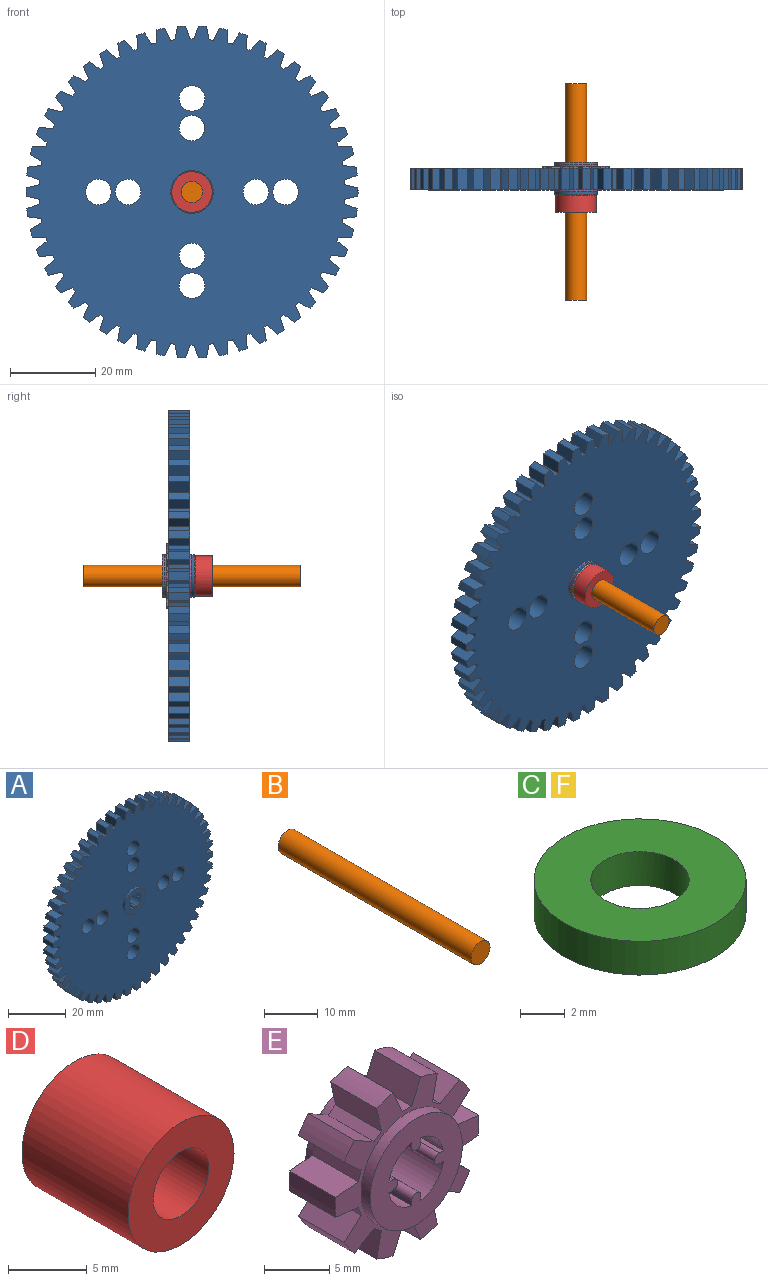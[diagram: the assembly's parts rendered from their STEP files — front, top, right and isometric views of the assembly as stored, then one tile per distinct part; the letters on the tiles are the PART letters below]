
ASSEMBLY  parts=6 mates=5
PART A: 230 faces, bbox 78x7x77.9 mm
  f0: plane 78x77.94mm, normal (0,1,0), area 4170.7mm2, adj f1,f3,f4,f5,f16,f26,f27,f28
  f1: cylinder r=3mm len=6mm, axis (0,1,0), area 94.2mm2, adj f0,f2
  f2: plane 78x77.94mm, normal (0,-1,0), area 4170.7mm2, adj f1,f3,f4,f5,f6,f26,f27,f28
  f3: cylinder r=3mm len=6mm, axis (0,1,0), area 94.2mm2, adj f0,f2
  f4: cylinder r=3mm len=6mm, axis (0,1,0), area 94.2mm2, adj f0,f2
  f5: cylinder r=3mm len=6mm, axis (0,1,0), area 94.2mm2, adj f0,f2
  f6: cylinder r=5mm len=10mm, axis (0,-1,0), area 31.4mm2, adj f2,f7
  f7: plane 10x10mm, normal (0,-1,0), area 53.8mm2, adj f6,f8,f9,f10,f11,f12,f13,f14
  f8: cylinder r=0.5mm len=7mm, axis (0,-1,0), area 11mm2, adj f7,f9,f14,f15
  f9: plane 7x0.46mm, normal (1,0,0), area 3.2mm2, adj f7,f8,f11,f15
  f10: cylinder r=3mm len=7mm, axis (0,1,0), area 26mm2, adj f7,f14,f15,f25
  f11: cylinder r=3mm len=7mm, axis (0,1,0), area 26mm2, adj f7,f9,f15,f17
  f12: cylinder r=3mm len=7mm, axis (0,1,0), area 26mm2, adj f7,f15,f19,f20
  f13: cylinder r=3mm len=7mm, axis (0,1,0), area 26mm2, adj f7,f15,f22,f23
  f14: plane 7x0.46mm, normal (-1,0,0), area 3.2mm2, adj f7,f8,f10,f15
  f15: plane 10x10mm, normal (0,1,0), area 53.8mm2, adj f8,f9,f10,f11,f12,f13,f14,f16
  f16: cylinder r=5mm len=10mm, axis (0,1,0), area 31.4mm2, adj f0,f15
  f17: plane 7x0.46mm, normal (0,0,1), area 3.2mm2, adj f7,f11,f15,f18
  f18: cylinder r=0.5mm len=7mm, axis (0,-1,0), area 11mm2, adj f7,f15,f17,f19
  f19: plane 7x0.46mm, normal (0,0,-1), area 3.2mm2, adj f7,f12,f15,f18
  f20: plane 7x0.46mm, normal (1,0,0), area 3.2mm2, adj f7,f12,f15,f21
  f21: cylinder r=0.5mm len=7mm, axis (0,-1,0), area 11mm2, adj f7,f15,f20,f22
  f22: plane 7x0.46mm, normal (-1,0,0), area 3.2mm2, adj f7,f13,f15,f21
  f23: plane 7x0.46mm, normal (0,0,-1), area 3.2mm2, adj f7,f13,f15,f24
  f24: cylinder r=0.5mm len=7mm, axis (0,-1,0), area 11mm2, adj f7,f15,f23,f25
  f25: plane 7x0.46mm, normal (0,0,1), area 3.2mm2, adj f7,f10,f15,f24
  f26: plane 5x0.99mm, normal (-0.13,0,0.99), area 5mm2, adj f0,f2,f27,f225
  f27: plane 5x3.1mm, normal (-0.98,0,0.19), area 15.8mm2, adj f0,f2,f26,f77
  f28: cylinder r=39mm len=5mm, axis (0,-1,0), area 9.5mm2, adj f0,f2,f78,f81
  f29: cylinder r=39mm len=5mm, axis (0,-1,0), area 9.5mm2, adj f0,f2,f80,f84
  f30: cylinder r=39mm len=5mm, axis (0,-1,0), area 9.5mm2, adj f0,f2,f86,f87
  f31: cylinder r=39mm len=5mm, axis (0,-1,0), area 9.5mm2, adj f0,f2,f89,f90
  f32: cylinder r=39mm len=5mm, axis (0,-1,0), area 9.5mm2, adj f0,f2,f92,f93
  f33: cylinder r=39mm len=5mm, axis (0,-1,0), area 9.5mm2, adj f0,f2,f95,f96
  f34: cylinder r=39mm len=5mm, axis (0,-1,0), area 9.5mm2, adj f0,f2,f98,f99
  f35: cylinder r=39mm len=5mm, axis (0,-1,0), area 9.5mm2, adj f0,f2,f101,f102
  f36: cylinder r=39mm len=5mm, axis (0,-1,0), area 9.5mm2, adj f0,f2,f104,f105
  f37: cylinder r=39mm len=5mm, axis (0,-1,0), area 9.5mm2, adj f0,f2,f107,f108
  f38: cylinder r=39mm len=5mm, axis (0,-1,0), area 9.5mm2, adj f0,f2,f110,f111
  f39: cylinder r=39mm len=5mm, axis (0,-1,0), area 9.5mm2, adj f0,f2,f113,f114
  f40: cylinder r=39mm len=5mm, axis (0,-1,0), area 9.5mm2, adj f0,f2,f116,f117
  f41: cylinder r=39mm len=5mm, axis (0,-1,0), area 9.5mm2, adj f0,f2,f119,f120
  f42: cylinder r=39mm len=5mm, axis (0,-1,0), area 9.5mm2, adj f0,f2,f122,f123
  f43: cylinder r=39mm len=5mm, axis (0,-1,0), area 9.5mm2, adj f0,f2,f125,f126
  f44: cylinder r=39mm len=5mm, axis (0,-1,0), area 9.5mm2, adj f0,f2,f128,f129
  f45: cylinder r=39mm len=5mm, axis (0,-1,0), area 9.5mm2, adj f0,f2,f131,f132
  f46: cylinder r=39mm len=5mm, axis (0,-1,0), area 9.5mm2, adj f0,f2,f134,f135
  f47: cylinder r=39mm len=5mm, axis (0,-1,0), area 9.5mm2, adj f0,f2,f137,f138
  f48: cylinder r=39mm len=5mm, axis (0,-1,0), area 9.5mm2, adj f0,f2,f140,f141
  f49: cylinder r=39mm len=5mm, axis (0,-1,0), area 9.5mm2, adj f0,f2,f143,f144
  f50: cylinder r=39mm len=5mm, axis (0,-1,0), area 9.5mm2, adj f0,f2,f146,f147
  f51: cylinder r=39mm len=5mm, axis (0,-1,0), area 9.5mm2, adj f0,f2,f149,f150
  f52: cylinder r=39mm len=5mm, axis (0,-1,0), area 9.5mm2, adj f0,f2,f152,f153
  f53: cylinder r=39mm len=5mm, axis (0,-1,0), area 9.5mm2, adj f0,f2,f155,f156
  f54: cylinder r=39mm len=5mm, axis (0,-1,0), area 9.5mm2, adj f0,f2,f158,f159
  f55: cylinder r=39mm len=5mm, axis (0,-1,0), area 9.5mm2, adj f0,f2,f161,f162
  f56: cylinder r=39mm len=5mm, axis (0,-1,0), area 9.5mm2, adj f0,f2,f164,f165
  f57: cylinder r=39mm len=5mm, axis (0,-1,0), area 9.5mm2, adj f0,f2,f167,f168
  f58: cylinder r=39mm len=5mm, axis (0,-1,0), area 9.5mm2, adj f0,f2,f170,f171
  f59: cylinder r=39mm len=5mm, axis (0,-1,0), area 9.5mm2, adj f0,f2,f173,f174
  f60: cylinder r=39mm len=5mm, axis (0,-1,0), area 9.5mm2, adj f0,f2,f176,f177
  f61: cylinder r=39mm len=5mm, axis (0,-1,0), area 9.5mm2, adj f0,f2,f179,f180
  f62: cylinder r=39mm len=5mm, axis (0,-1,0), area 9.5mm2, adj f0,f2,f182,f183
  f63: cylinder r=39mm len=5mm, axis (0,-1,0), area 9.5mm2, adj f0,f2,f185,f186
  f64: cylinder r=39mm len=5mm, axis (0,-1,0), area 9.5mm2, adj f0,f2,f188,f189
  f65: cylinder r=39mm len=5mm, axis (0,-1,0), area 9.5mm2, adj f0,f2,f191,f192
  f66: cylinder r=39mm len=5mm, axis (0,-1,0), area 9.5mm2, adj f0,f2,f194,f195
  f67: cylinder r=39mm len=5mm, axis (0,-1,0), area 9.5mm2, adj f0,f2,f197,f198
  f68: cylinder r=39mm len=5mm, axis (0,-1,0), area 9.5mm2, adj f0,f2,f200,f201
  f69: cylinder r=39mm len=5mm, axis (0,-1,0), area 9.5mm2, adj f0,f2,f203,f204
  f70: cylinder r=39mm len=5mm, axis (0,-1,0), area 9.5mm2, adj f0,f2,f206,f207
  f71: cylinder r=39mm len=5mm, axis (0,-1,0), area 9.5mm2, adj f0,f2,f209,f210
  f72: cylinder r=39mm len=5mm, axis (0,-1,0), area 9.5mm2, adj f0,f2,f212,f213
  f73: cylinder r=39mm len=5mm, axis (0,-1,0), area 9.5mm2, adj f0,f2,f215,f216
  f74: cylinder r=39mm len=5mm, axis (0,-1,0), area 9.5mm2, adj f0,f2,f218,f219
  f75: cylinder r=39mm len=5mm, axis (0,-1,0), area 9.5mm2, adj f0,f2,f221,f222
  f76: cylinder r=39mm len=5mm, axis (0,-1,0), area 9.5mm2, adj f0,f2,f224,f225
  f77: cylinder r=39mm len=5mm, axis (0,-1,0), area 9.5mm2, adj f0,f2,f27,f83
  f78: plane 5x3.1mm, normal (0.98,0,0.19), area 15.8mm2, adj f0,f2,f28,f79
  f79: plane 5x0.99mm, normal (0.13,0,0.99), area 5mm2, adj f0,f2,f78,f80
  f80: plane 5x2.85mm, normal (-0.9,0,0.43), area 15.8mm2, adj f0,f2,f29,f79
  f81: plane 5x3mm, normal (-0.95,0,0.32), area 15.8mm2, adj f0,f2,f28,f82
  f82: plane 5x1mm, normal (0,0,1), area 5mm2, adj f0,f2,f81,f83
  f83: plane 5x3mm, normal (0.95,0,0.32), area 15.8mm2, adj f0,f2,f77,f82
  f84: plane 5x3.15mm, normal (1,0,0.07), area 15.8mm2, adj f0,f2,f29,f85
  f85: plane 5x0.97mm, normal (0.25,0,0.97), area 5mm2, adj f0,f2,f84,f86
  f86: plane 5x2.66mm, normal (-0.84,0,0.54), area 15.8mm2, adj f0,f2,f30,f85
  f87: plane 5x3.16mm, normal (1,0,-0.06), area 15.8mm2, adj f0,f2,f30,f88
  f88: plane 5x0.93mm, normal (0.37,0,0.93), area 5mm2, adj f0,f2,f87,f89
  f89: plane 5x2.42mm, normal (-0.77,0,0.64), area 15.8mm2, adj f0,f2,f31,f88
  f90: plane 5x3.11mm, normal (0.98,0,-0.18), area 15.8mm2, adj f0,f2,f31,f91
  f91: plane 5x0.88mm, normal (0.48,0,0.88), area 5mm2, adj f0,f2,f90,f92
  f92: plane 5x2.32mm, normal (-0.68,0,0.73), area 15.8mm2, adj f0,f2,f32,f91
  f93: plane 5x3.02mm, normal (0.95,0,-0.3), area 15.8mm2, adj f0,f2,f32,f94
  f94: plane 5x0.81mm, normal (0.59,0,0.81), area 5mm2, adj f0,f2,f93,f95
  f95: plane 5x2.57mm, normal (-0.58,0,0.81), area 15.8mm2, adj f0,f2,f33,f94
  f96: plane 5x2.87mm, normal (0.91,0,-0.42), area 15.8mm2, adj f0,f2,f33,f97
  f97: plane 5x0.73mm, normal (0.68,0,0.73), area 5mm2, adj f0,f2,f96,f98
  f98: plane 5x2.78mm, normal (-0.48,0,0.88), area 15.8mm2, adj f0,f2,f34,f97
  f99: plane 5x2.68mm, normal (0.85,0,-0.53), area 15.8mm2, adj f0,f2,f34,f100
  f100: plane 5x0.77mm, normal (0.77,0,0.64), area 5mm2, adj f0,f2,f99,f101
  f101: plane 5x2.95mm, normal (-0.36,0,0.93), area 15.8mm2, adj f0,f2,f35,f100
  f102: plane 5x2.45mm, normal (0.78,0,-0.63), area 15.8mm2, adj f0,f2,f35,f103
  f103: plane 5x0.84mm, normal (0.84,0,0.54), area 5mm2, adj f0,f2,f102,f104
  f104: plane 5x3.07mm, normal (-0.24,0,0.97), area 15.8mm2, adj f0,f2,f36,f103
  f105: plane 5x2.29mm, normal (0.69,0,-0.72), area 15.8mm2, adj f0,f2,f36,f106
  f106: plane 5x0.91mm, normal (0.9,0,0.43), area 5mm2, adj f0,f2,f105,f107
  f107: plane 5x3.14mm, normal (-0.12,0,0.99), area 15.8mm2, adj f0,f2,f37,f106
  f108: plane 5x2.54mm, normal (0.59,0,-0.8), area 15.8mm2, adj f0,f2,f37,f109
  f109: plane 5x0.95mm, normal (0.95,0,0.31), area 5mm2, adj f0,f2,f108,f110
  f110: plane 5x3.16mm, normal (0.01,0,1), area 15.8mm2, adj f0,f2,f38,f109
  f111: plane 5x2.76mm, normal (0.49,0,-0.87), area 15.8mm2, adj f0,f2,f38,f112
  f112: plane 5x0.98mm, normal (0.98,0,0.19), area 5mm2, adj f0,f2,f111,f113
  f113: plane 5x3.13mm, normal (0.13,0,0.99), area 15.8mm2, adj f0,f2,f39,f112
  f114: plane 5x2.93mm, normal (0.38,0,-0.93), area 15.8mm2, adj f0,f2,f39,f115
  f115: plane 5x1mm, normal (1,0,0.06), area 5mm2, adj f0,f2,f114,f116
  f116: plane 5x3.06mm, normal (0.26,0,0.97), area 15.8mm2, adj f0,f2,f40,f115
  f117: plane 5x3.06mm, normal (0.26,0,-0.97), area 15.8mm2, adj f0,f2,f40,f118
  f118: plane 5x1mm, normal (1,0,-0.06), area 5mm2, adj f0,f2,f117,f119
  f119: plane 5x2.93mm, normal (0.38,0,0.93), area 15.8mm2, adj f0,f2,f41,f118
  f120: plane 5x3.13mm, normal (0.13,0,-0.99), area 15.8mm2, adj f0,f2,f41,f121
  f121: plane 5x0.98mm, normal (0.98,0,-0.19), area 5mm2, adj f0,f2,f120,f122
  f122: plane 5x2.76mm, normal (0.49,0,0.87), area 15.8mm2, adj f0,f2,f42,f121
  f123: plane 5x3.16mm, normal (0.01,0,-1), area 15.8mm2, adj f0,f2,f42,f124
  f124: plane 5x0.95mm, normal (0.95,0,-0.31), area 5mm2, adj f0,f2,f123,f125
  f125: plane 5x2.54mm, normal (0.59,0,0.8), area 15.8mm2, adj f0,f2,f43,f124
  f126: plane 5x3.14mm, normal (-0.12,0,-0.99), area 15.8mm2, adj f0,f2,f43,f127
  f127: plane 5x0.91mm, normal (0.9,0,-0.43), area 5mm2, adj f0,f2,f126,f128
  f128: plane 5x2.29mm, normal (0.69,0,0.72), area 15.8mm2, adj f0,f2,f44,f127
  f129: plane 5x3.07mm, normal (-0.24,0,-0.97), area 15.8mm2, adj f0,f2,f44,f130
  f130: plane 5x0.84mm, normal (0.84,0,-0.54), area 5mm2, adj f0,f2,f129,f131
  f131: plane 5x2.45mm, normal (0.78,0,0.63), area 15.8mm2, adj f0,f2,f45,f130
  f132: plane 5x2.95mm, normal (-0.36,0,-0.93), area 15.8mm2, adj f0,f2,f45,f133
  f133: plane 5x0.77mm, normal (0.77,0,-0.64), area 5mm2, adj f0,f2,f132,f134
  f134: plane 5x2.68mm, normal (0.85,0,0.53), area 15.8mm2, adj f0,f2,f46,f133
  f135: plane 5x2.78mm, normal (-0.48,0,-0.88), area 15.8mm2, adj f0,f2,f46,f136
  f136: plane 5x0.73mm, normal (0.68,0,-0.73), area 5mm2, adj f0,f2,f135,f137
  f137: plane 5x2.87mm, normal (0.91,0,0.42), area 15.8mm2, adj f0,f2,f47,f136
  f138: plane 5x2.57mm, normal (-0.58,0,-0.81), area 15.8mm2, adj f0,f2,f47,f139
  f139: plane 5x0.81mm, normal (0.59,0,-0.81), area 5mm2, adj f0,f2,f138,f140
  f140: plane 5x3.02mm, normal (0.95,0,0.3), area 15.8mm2, adj f0,f2,f48,f139
  f141: plane 5x2.32mm, normal (-0.68,0,-0.73), area 15.8mm2, adj f0,f2,f48,f142
  f142: plane 5x0.88mm, normal (0.48,0,-0.88), area 5mm2, adj f0,f2,f141,f143
  f143: plane 5x3.11mm, normal (0.98,0,0.18), area 15.8mm2, adj f0,f2,f49,f142
  f144: plane 5x2.42mm, normal (-0.77,0,-0.64), area 15.8mm2, adj f0,f2,f49,f145
  f145: plane 5x0.93mm, normal (0.37,0,-0.93), area 5mm2, adj f0,f2,f144,f146
  f146: plane 5x3.16mm, normal (1,0,0.06), area 15.8mm2, adj f0,f2,f50,f145
  f147: plane 5x2.66mm, normal (-0.84,0,-0.54), area 15.8mm2, adj f0,f2,f50,f148
  f148: plane 5x0.97mm, normal (0.25,0,-0.97), area 5mm2, adj f0,f2,f147,f149
  f149: plane 5x3.15mm, normal (1,0,-0.07), area 15.8mm2, adj f0,f2,f51,f148
  f150: plane 5x2.85mm, normal (-0.9,0,-0.43), area 15.8mm2, adj f0,f2,f51,f151
  f151: plane 5x0.99mm, normal (0.13,0,-0.99), area 5mm2, adj f0,f2,f150,f152
  f152: plane 5x3.1mm, normal (0.98,0,-0.19), area 15.8mm2, adj f0,f2,f52,f151
  f153: plane 5x3mm, normal (-0.95,0,-0.32), area 15.8mm2, adj f0,f2,f52,f154
  f154: plane 5x1mm, normal (0,0,-1), area 5mm2, adj f0,f2,f153,f155
  f155: plane 5x3mm, normal (0.95,0,-0.32), area 15.8mm2, adj f0,f2,f53,f154
  f156: plane 5x3.1mm, normal (-0.98,0,-0.19), area 15.8mm2, adj f0,f2,f53,f157
  f157: plane 5x0.99mm, normal (-0.13,0,-0.99), area 5mm2, adj f0,f2,f156,f158
  f158: plane 5x2.85mm, normal (0.9,0,-0.43), area 15.8mm2, adj f0,f2,f54,f157
  f159: plane 5x3.15mm, normal (-1,0,-0.07), area 15.8mm2, adj f0,f2,f54,f160
  f160: plane 5x0.97mm, normal (-0.25,0,-0.97), area 5mm2, adj f0,f2,f159,f161
  f161: plane 5x2.66mm, normal (0.84,0,-0.54), area 15.8mm2, adj f0,f2,f55,f160
  f162: plane 5x3.16mm, normal (-1,0,0.06), area 15.8mm2, adj f0,f2,f55,f163
  f163: plane 5x0.93mm, normal (-0.37,0,-0.93), area 5mm2, adj f0,f2,f162,f164
  f164: plane 5x2.42mm, normal (0.77,0,-0.64), area 15.8mm2, adj f0,f2,f56,f163
  f165: plane 5x3.11mm, normal (-0.98,0,0.18), area 15.8mm2, adj f0,f2,f56,f166
  f166: plane 5x0.88mm, normal (-0.48,0,-0.88), area 5mm2, adj f0,f2,f165,f167
  f167: plane 5x2.32mm, normal (0.68,0,-0.73), area 15.8mm2, adj f0,f2,f57,f166
  f168: plane 5x3.02mm, normal (-0.95,0,0.3), area 15.8mm2, adj f0,f2,f57,f169
  f169: plane 5x0.81mm, normal (-0.59,0,-0.81), area 5mm2, adj f0,f2,f168,f170
  f170: plane 5x2.57mm, normal (0.58,0,-0.81), area 15.8mm2, adj f0,f2,f58,f169
  f171: plane 5x2.87mm, normal (-0.91,0,0.42), area 15.8mm2, adj f0,f2,f58,f172
  f172: plane 5x0.73mm, normal (-0.68,0,-0.73), area 5mm2, adj f0,f2,f171,f173
  f173: plane 5x2.78mm, normal (0.48,0,-0.88), area 15.8mm2, adj f0,f2,f59,f172
  f174: plane 5x2.68mm, normal (-0.85,0,0.53), area 15.8mm2, adj f0,f2,f59,f175
  f175: plane 5x0.77mm, normal (-0.77,0,-0.64), area 5mm2, adj f0,f2,f174,f176
  f176: plane 5x2.95mm, normal (0.36,0,-0.93), area 15.8mm2, adj f0,f2,f60,f175
  f177: plane 5x2.45mm, normal (-0.78,0,0.63), area 15.8mm2, adj f0,f2,f60,f178
  f178: plane 5x0.84mm, normal (-0.84,0,-0.54), area 5mm2, adj f0,f2,f177,f179
  f179: plane 5x3.07mm, normal (0.24,0,-0.97), area 15.8mm2, adj f0,f2,f61,f178
  f180: plane 5x2.29mm, normal (-0.69,0,0.72), area 15.8mm2, adj f0,f2,f61,f181
  f181: plane 5x0.91mm, normal (-0.9,0,-0.43), area 5mm2, adj f0,f2,f180,f182
  f182: plane 5x3.14mm, normal (0.12,0,-0.99), area 15.8mm2, adj f0,f2,f62,f181
  f183: plane 5x2.54mm, normal (-0.59,0,0.8), area 15.8mm2, adj f0,f2,f62,f184
  f184: plane 5x0.95mm, normal (-0.95,0,-0.31), area 5mm2, adj f0,f2,f183,f185
  f185: plane 5x3.16mm, normal (-0.01,0,-1), area 15.8mm2, adj f0,f2,f63,f184
  f186: plane 5x2.76mm, normal (-0.49,0,0.87), area 15.8mm2, adj f0,f2,f63,f187
  f187: plane 5x0.98mm, normal (-0.98,0,-0.19), area 5mm2, adj f0,f2,f186,f188
  f188: plane 5x3.13mm, normal (-0.13,0,-0.99), area 15.8mm2, adj f0,f2,f64,f187
  f189: plane 5x2.93mm, normal (-0.38,0,0.93), area 15.8mm2, adj f0,f2,f64,f190
  f190: plane 5x1mm, normal (-1,0,-0.06), area 5mm2, adj f0,f2,f189,f191
  f191: plane 5x3.06mm, normal (-0.26,0,-0.97), area 15.8mm2, adj f0,f2,f65,f190
  f192: plane 5x3.06mm, normal (-0.26,0,0.97), area 15.8mm2, adj f0,f2,f65,f193
  f193: plane 5x1mm, normal (-1,0,0.06), area 5mm2, adj f0,f2,f192,f194
  f194: plane 5x2.93mm, normal (-0.38,0,-0.93), area 15.8mm2, adj f0,f2,f66,f193
  f195: plane 5x3.13mm, normal (-0.13,0,0.99), area 15.8mm2, adj f0,f2,f66,f196
  f196: plane 5x0.98mm, normal (-0.98,0,0.19), area 5mm2, adj f0,f2,f195,f197
  f197: plane 5x2.76mm, normal (-0.49,0,-0.87), area 15.8mm2, adj f0,f2,f67,f196
  f198: plane 5x3.16mm, normal (-0.01,0,1), area 15.8mm2, adj f0,f2,f67,f199
  f199: plane 5x0.95mm, normal (-0.95,0,0.31), area 5mm2, adj f0,f2,f198,f200
  f200: plane 5x2.54mm, normal (-0.59,0,-0.8), area 15.8mm2, adj f0,f2,f68,f199
  f201: plane 5x3.14mm, normal (0.12,0,0.99), area 15.8mm2, adj f0,f2,f68,f202
  f202: plane 5x0.91mm, normal (-0.9,0,0.43), area 5mm2, adj f0,f2,f201,f203
  f203: plane 5x2.29mm, normal (-0.69,0,-0.72), area 15.8mm2, adj f0,f2,f69,f202
  f204: plane 5x3.07mm, normal (0.24,0,0.97), area 15.8mm2, adj f0,f2,f69,f205
  f205: plane 5x0.84mm, normal (-0.84,0,0.54), area 5mm2, adj f0,f2,f204,f206
  f206: plane 5x2.45mm, normal (-0.78,0,-0.63), area 15.8mm2, adj f0,f2,f70,f205
  f207: plane 5x2.95mm, normal (0.36,0,0.93), area 15.8mm2, adj f0,f2,f70,f208
  f208: plane 5x0.77mm, normal (-0.77,0,0.64), area 5mm2, adj f0,f2,f207,f209
  f209: plane 5x2.68mm, normal (-0.85,0,-0.53), area 15.8mm2, adj f0,f2,f71,f208
  f210: plane 5x2.78mm, normal (0.48,0,0.88), area 15.8mm2, adj f0,f2,f71,f211
  f211: plane 5x0.73mm, normal (-0.68,0,0.73), area 5mm2, adj f0,f2,f210,f212
  f212: plane 5x2.87mm, normal (-0.91,0,-0.42), area 15.8mm2, adj f0,f2,f72,f211
  f213: plane 5x2.57mm, normal (0.58,0,0.81), area 15.8mm2, adj f0,f2,f72,f214
  f214: plane 5x0.81mm, normal (-0.59,0,0.81), area 5mm2, adj f0,f2,f213,f215
  f215: plane 5x3.02mm, normal (-0.95,0,-0.3), area 15.8mm2, adj f0,f2,f73,f214
  f216: plane 5x2.32mm, normal (0.68,0,0.73), area 15.8mm2, adj f0,f2,f73,f217
  f217: plane 5x0.88mm, normal (-0.48,0,0.88), area 5mm2, adj f0,f2,f216,f218
  f218: plane 5x3.11mm, normal (-0.98,0,-0.18), area 15.8mm2, adj f0,f2,f74,f217
  f219: plane 5x2.42mm, normal (0.77,0,0.64), area 15.8mm2, adj f0,f2,f74,f220
  f220: plane 5x0.93mm, normal (-0.37,0,0.93), area 5mm2, adj f0,f2,f219,f221
  f221: plane 5x3.16mm, normal (-1,0,-0.06), area 15.8mm2, adj f0,f2,f75,f220
  f222: plane 5x2.66mm, normal (0.84,0,0.54), area 15.8mm2, adj f0,f2,f75,f223
  f223: plane 5x0.97mm, normal (-0.25,0,0.97), area 5mm2, adj f0,f2,f222,f224
  f224: plane 5x3.15mm, normal (-1,0,0.07), area 15.8mm2, adj f0,f2,f76,f223
  f225: plane 5x2.85mm, normal (0.9,0,0.43), area 15.8mm2, adj f0,f2,f26,f76
  f226: cylinder r=3mm len=6mm, axis (0,-1,0), area 94.2mm2, adj f0,f2
  f227: cylinder r=3mm len=6mm, axis (0,-1,0), area 94.2mm2, adj f0,f2
  f228: cylinder r=3mm len=6mm, axis (0,-1,0), area 94.2mm2, adj f0,f2
  f229: cylinder r=3mm len=6mm, axis (0,-1,0), area 94.2mm2, adj f0,f2
PART B: 3 faces, bbox 5x50.8x5 mm
  f0: cylinder r=2.5mm len=50.8mm, axis (0,1,0), area 798mm2, adj f1,f2
  f1: plane 5x5mm, normal (0,-1,0), area 19.6mm2, adj f0
  f2: plane 5x5mm, normal (0,1,0), area 19.6mm2, adj f0
PART C: 4 faces, bbox 9.5x9.5x1.9 mm
  f0: cylinder r=2.21mm len=4.42mm, axis (0,0,1), area 25.7mm2, adj f1,f3
  f1: plane 9.53x9.53mm, normal (0,0,-1), area 55.9mm2, adj f0,f2
  f2: cylinder r=4.76mm len=9.53mm, axis (0,0,-1), area 55.5mm2, adj f1,f3
  f3: plane 9.53x9.53mm, normal (0,0,1), area 55.9mm2, adj f0,f2
PART D: 4 faces, bbox 9.5x9.5x9.5 mm
  f0: cylinder r=2.5mm len=9.53mm, axis (0,1,0), area 149.6mm2, adj f2,f3
  f1: cylinder r=4.76mm len=9.53mm, axis (0,1,0), area 285mm2, adj f2,f3
  f2: plane 9.53x9.53mm, normal (0,-1,0), area 51.6mm2, adj f0,f1
  f3: plane 9.53x9.53mm, normal (0,1,0), area 51.6mm2, adj f0,f1
PART E: 62 faces, bbox 15.6x7x15.3 mm
  f0: plane 15.6x15.31mm, normal (0,1,0), area 64.7mm2, adj f1,f7,f8,f9,f10,f11,f12,f13
  f1: cylinder r=5mm len=10mm, axis (0,1,0), area 31.4mm2, adj f0,f2
  f2: plane 10x10mm, normal (0,1,0), area 53.8mm2, adj f1,f3,f47,f48,f49,f50,f51,f52
  f3: cylinder r=0.5mm len=7mm, axis (0,-1,0), area 11mm2, adj f2,f4,f47,f58
  f4: plane 10x10mm, normal (0,-1,0), area 53.8mm2, adj f3,f5,f47,f48,f49,f50,f51,f52
  f5: cylinder r=5mm len=10mm, axis (0,-1,0), area 31.4mm2, adj f4,f6
  f6: plane 15.6x15.31mm, normal (0,-1,0), area 64.7mm2, adj f5,f7,f8,f9,f10,f11,f12,f13
  f7: plane 5x0.81mm, normal (-0.59,0,0.81), area 5mm2, adj f0,f6,f8,f46
  f8: plane 5x2.41mm, normal (-0.98,0,-0.21), area 12.3mm2, adj f0,f6,f7,f18
  f9: cylinder r=7.8mm len=5mm, axis (0,-1,0), area 9.4mm2, adj f0,f6,f19,f22
  f10: cylinder r=7.8mm len=5mm, axis (0,-1,0), area 9.4mm2, adj f0,f6,f21,f25
  f11: cylinder r=7.8mm len=5mm, axis (0,-1,0), area 9.4mm2, adj f0,f6,f27,f28
  f12: cylinder r=7.8mm len=5mm, axis (0,-1,0), area 9.4mm2, adj f0,f6,f30,f31
  f13: cylinder r=7.8mm len=5mm, axis (0,-1,0), area 9.4mm2, adj f0,f6,f33,f34
  f14: cylinder r=7.8mm len=5mm, axis (0,-1,0), area 9.4mm2, adj f0,f6,f36,f37
  f15: cylinder r=7.8mm len=5mm, axis (0,-1,0), area 9.4mm2, adj f0,f6,f39,f40
  f16: cylinder r=7.8mm len=5mm, axis (0,-1,0), area 9.4mm2, adj f0,f6,f42,f43
  f17: cylinder r=7.8mm len=5mm, axis (0,-1,0), area 9.4mm2, adj f0,f6,f45,f46
  f18: cylinder r=7.8mm len=5mm, axis (0,-1,0), area 9.4mm2, adj f0,f6,f8,f24
  f19: plane 5x2.41mm, normal (0.98,0,-0.21), area 12.3mm2, adj f0,f6,f9,f20
  f20: plane 5x0.81mm, normal (0.59,0,0.81), area 5mm2, adj f0,f6,f19,f21
  f21: plane 5x2.13mm, normal (-0.5,0,0.87), area 12.3mm2, adj f0,f6,f10,f20
  f22: plane 5x2.25mm, normal (-0.91,0,0.41), area 12.3mm2, adj f0,f6,f9,f23
  f23: plane 5x1mm, normal (0,0,1), area 5mm2, adj f0,f6,f22,f24
  f24: plane 5x2.25mm, normal (0.91,0,0.41), area 12.3mm2, adj f0,f6,f18,f23
  f25: plane 5x1.83mm, normal (0.67,0,-0.74), area 12.3mm2, adj f0,f6,f10,f26
  f26: plane 5x0.95mm, normal (0.95,0,0.31), area 5mm2, adj f0,f6,f25,f27
  f27: plane 5x2.45mm, normal (0.1,0,0.99), area 12.3mm2, adj f0,f6,f11,f26
  f28: plane 5x2.45mm, normal (0.1,0,-0.99), area 12.3mm2, adj f0,f6,f11,f29
  f29: plane 5x0.95mm, normal (0.95,0,-0.31), area 5mm2, adj f0,f6,f28,f30
  f30: plane 5x1.83mm, normal (0.67,0,0.74), area 12.3mm2, adj f0,f6,f12,f29
  f31: plane 5x2.13mm, normal (-0.5,0,-0.87), area 12.3mm2, adj f0,f6,f12,f32
  f32: plane 5x0.81mm, normal (0.59,0,-0.81), area 5mm2, adj f0,f6,f31,f33
  f33: plane 5x2.41mm, normal (0.98,0,0.21), area 12.3mm2, adj f0,f6,f13,f32
  f34: plane 5x2.25mm, normal (-0.91,0,-0.41), area 12.3mm2, adj f0,f6,f13,f35
  f35: plane 5x1mm, normal (0,0,-1), area 5mm2, adj f0,f6,f34,f36
  f36: plane 5x2.25mm, normal (0.91,0,-0.41), area 12.3mm2, adj f0,f6,f14,f35
  f37: plane 5x2.41mm, normal (-0.98,0,0.21), area 12.3mm2, adj f0,f6,f14,f38
  f38: plane 5x0.81mm, normal (-0.59,0,-0.81), area 5mm2, adj f0,f6,f37,f39
  f39: plane 5x2.13mm, normal (0.5,0,-0.87), area 12.3mm2, adj f0,f6,f15,f38
  f40: plane 5x1.83mm, normal (-0.67,0,0.74), area 12.3mm2, adj f0,f6,f15,f41
  f41: plane 5x0.95mm, normal (-0.95,0,-0.31), area 5mm2, adj f0,f6,f40,f42
  f42: plane 5x2.45mm, normal (-0.1,0,-0.99), area 12.3mm2, adj f0,f6,f16,f41
  f43: plane 5x2.45mm, normal (-0.1,0,0.99), area 12.3mm2, adj f0,f6,f16,f44
  f44: plane 5x0.95mm, normal (-0.95,0,0.31), area 5mm2, adj f0,f6,f43,f45
  f45: plane 5x1.83mm, normal (-0.67,0,-0.74), area 12.3mm2, adj f0,f6,f17,f44
  f46: plane 5x2.13mm, normal (0.5,0,0.87), area 12.3mm2, adj f0,f6,f7,f17
  f47: plane 7x0.46mm, normal (-1,0,0), area 3.2mm2, adj f2,f3,f4,f48
  f48: cylinder r=3mm len=7mm, axis (0,1,0), area 26mm2, adj f2,f4,f47,f52
  f49: cylinder r=3mm len=7mm, axis (0,1,0), area 26mm2, adj f2,f4,f55,f58
  f50: cylinder r=3mm len=7mm, axis (0,1,0), area 26mm2, adj f2,f4,f57,f59
  f51: cylinder r=3mm len=7mm, axis (0,1,0), area 26mm2, adj f2,f4,f54,f61
  f52: plane 7x0.46mm, normal (0,0,1), area 3.2mm2, adj f2,f4,f48,f53
  f53: cylinder r=0.5mm len=7mm, axis (0,-1,0), area 11mm2, adj f2,f4,f52,f54
  f54: plane 7x0.46mm, normal (0,0,-1), area 3.2mm2, adj f2,f4,f51,f53
  f55: plane 7x0.46mm, normal (0,0,1), area 3.2mm2, adj f2,f4,f49,f56
  f56: cylinder r=0.5mm len=7mm, axis (0,-1,0), area 11mm2, adj f2,f4,f55,f57
  f57: plane 7x0.46mm, normal (0,0,-1), area 3.2mm2, adj f2,f4,f50,f56
  f58: plane 7x0.46mm, normal (1,0,0), area 3.2mm2, adj f2,f3,f4,f49
  f59: plane 7x0.46mm, normal (1,0,0), area 3.2mm2, adj f2,f4,f50,f60
  f60: cylinder r=0.5mm len=7mm, axis (0,-1,0), area 11mm2, adj f2,f4,f59,f61
  f61: plane 7x0.46mm, normal (-1,0,0), area 3.2mm2, adj f2,f4,f51,f60
PART F: same geometry as C
PLACE A t=(-10.9,-2.62,-2.75)mm
PLACE B t=(-43.86,17.28,-64.09)mm
PLACE C rot(axis=(1,0,0),90deg) t=(-10.9,-7.2,-2.75)mm
PLACE D t=(-10.9,-3.36,-2.75)mm
PLACE E t=(-10.9,-2.12,-2.75)mm
PLACE F rot(axis=(1,0,0),90deg) t=(-10.9,-7.2,-2.75)mm
MATE cylindrical D.f0 <-> B.f0  axis (0,1,0) through (-10.9,-8.12,-2.75)mm
MATE cylindrical F.f0 <-> B.f0  axis (0,1,0) through (-10.9,-8.12,-2.75)mm
MATE cylindrical C.f0 <-> B.f0  axis (0,1,0) through (-10.9,-8.12,-2.75)mm
MATE cylindrical A.f6 <-> B.f0  axis (0,-1,0) through (-10.9,-8.12,-2.75)mm
MATE cylindrical E.f1 <-> B.f0  axis (0,-1,0) through (-10.9,-8.12,-2.75)mm
